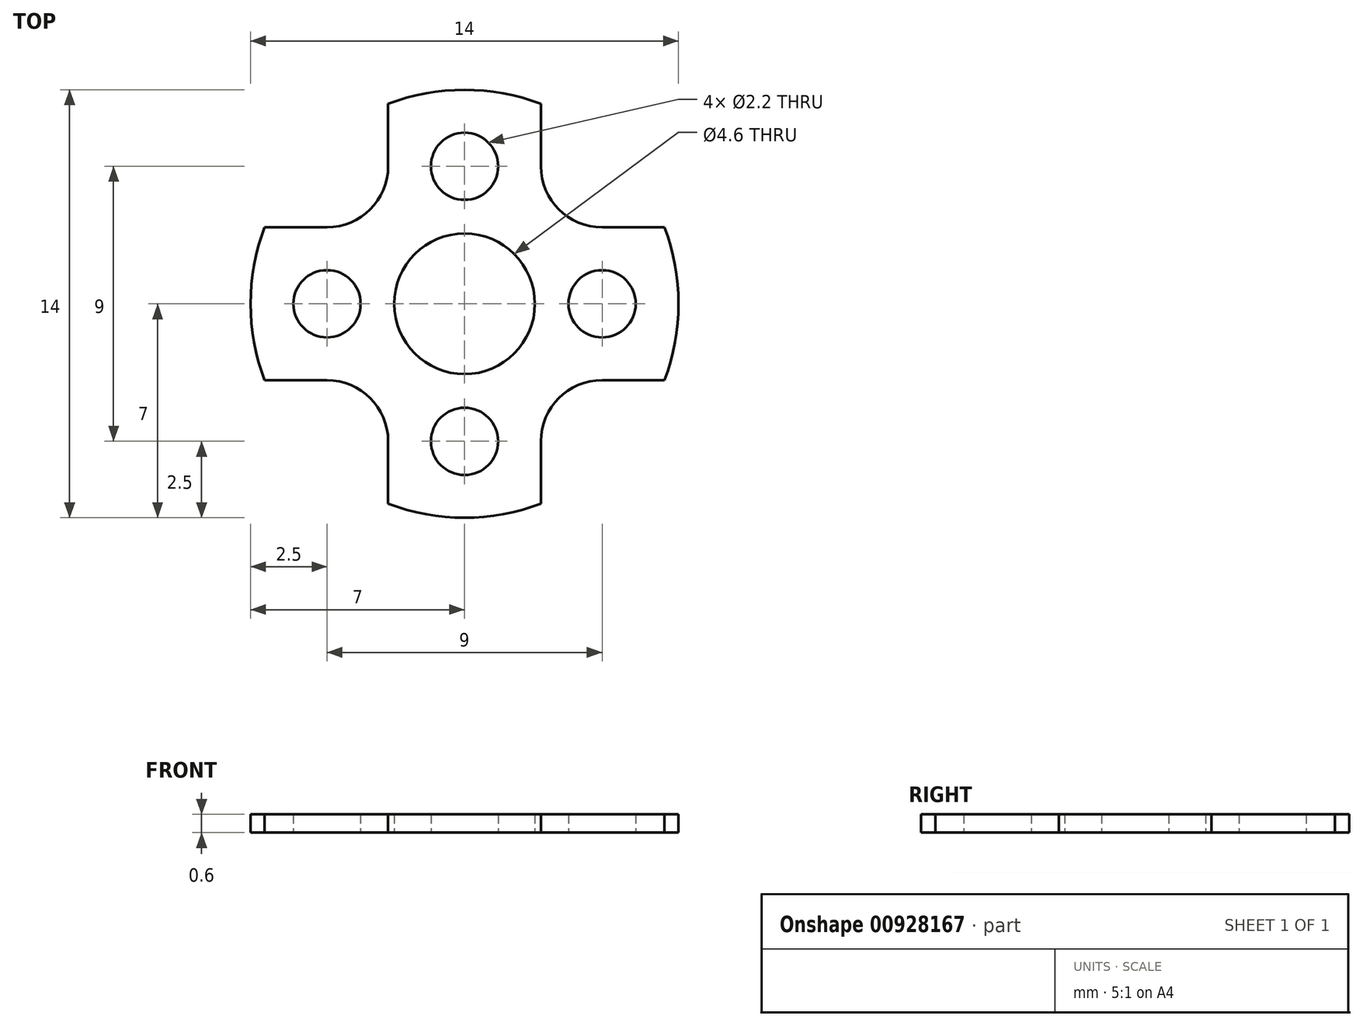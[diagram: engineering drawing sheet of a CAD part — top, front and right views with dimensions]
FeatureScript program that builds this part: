
annotation { "Feature Type Name" : "Feature", "Feature Type Description" : "" }
export const myFeature = defineFeature(function(context is Context, id is Id, definition is map)
    precondition{}
    {
        {
            var Q0;
            Q0=qCreatedBy(makeId("Top.planeOp"),FACE);
            var sketch = newSketch(context, id + "F0", { "sketchPlane" : qUnion([Q0])});
            skArc(sketch, "E0", {"start": v(2.5, 6.54) * mm, "mid": v(0, 7) * mm, "end": v(-2.5, 6.54) * mm});
            skPoint(sketch, "E1", {"position": v(4.5, 4.5) * mm});
            skCircle(sketch, "E2", {"center": v(0, 4.5) * mm, "radius": 1.1 * mm});
            skCircle(sketch, "E3", {"center": v(-4.5, 0) * mm, "radius": 1.1 * mm});
            skCircle(sketch, "E4", {"center": v(0, -4.5) * mm, "radius": 1.1 * mm});
            skCircle(sketch, "E5", {"center": v(4.5, 0) * mm, "radius": 1.1 * mm});
            skArc(sketch, "E6", {"start": v(2.5, 4.5) * mm, "mid": v(3.09, 3.09) * mm, "end": v(4.5, 2.5) * mm});
            skLineSegment(sketch, "E7", {"start": v(2.5, 4.5) * mm, "end": v(2.5, 6.54) * mm});
            skLineSegment(sketch, "E8", {"start": v(4.5, 2.5) * mm, "end": v(6.54, 2.5) * mm});
            skCircle(sketch, "E9", {"center": v(0, 0) * mm, "radius": 2.3 * mm});
            skArc(sketch, "E10", {"start": v(-4.5, 2.5) * mm, "mid": v(-3.09, 3.09) * mm, "end": v(-2.5, 4.5) * mm});
            skArc(sketch, "E11", {"start": v(-2.5, -4.5) * mm, "mid": v(-3.09, -3.09) * mm, "end": v(-4.5, -2.5) * mm});
            skArc(sketch, "E12", {"start": v(4.5, -2.5) * mm, "mid": v(3.09, -3.09) * mm, "end": v(2.5, -4.5) * mm});
            skLineSegment(sketch, "E13", {"start": v(-4.5, 2.5) * mm, "end": v(-6.54, 2.5) * mm});
            skLineSegment(sketch, "E14", {"start": v(-2.5, 4.5) * mm, "end": v(-2.5, 6.54) * mm});
            skLineSegment(sketch, "E15", {"start": v(-2.5, -4.5) * mm, "end": v(-2.5, -6.54) * mm});
            skLineSegment(sketch, "E16", {"start": v(-4.5, -2.5) * mm, "end": v(-6.54, -2.5) * mm});
            skLineSegment(sketch, "E17", {"start": v(2.5, -4.5) * mm, "end": v(2.5, -6.54) * mm});
            skLineSegment(sketch, "E18", {"start": v(4.5, -2.5) * mm, "end": v(6.54, -2.5) * mm});
            skArc(sketch, "E19.trimOffspring", {"start": v(-6.54, 2.5) * mm, "mid": v(-7, 0) * mm, "end": v(-6.54, -2.5) * mm});
            skArc(sketch, "E20.trimOffspring", {"start": v(6.54, -2.5) * mm, "mid": v(7, 0) * mm, "end": v(6.54, 2.5) * mm});
            skArc(sketch, "E21.trimOffspring", {"start": v(-2.5, -6.54) * mm, "mid": v(0, -7) * mm, "end": v(2.5, -6.54) * mm});
            skSolve(sketch);
        }
        {
            var Q0;
            Q0=makeQuery(id+"F0.imprint","IMPRINT",FACE,{"disambiguationData":[TD([[makeQuery(id+"F0.imprint","IMPRINT",EDGE,{"derivedFrom":sQuery(id+"F0.wireOp",EDGE,"E0")}),1.0]])]});
            extrude(context, id + "F1", {"entities" : qUnion([Q0]), "depth" : 0.6 * mm, "offsetDistance" : 25 * mm});
        }
    });
